# Revit family: Edge S - OX+
name_source: partatom
category: Doors
units: mm (PartAtom-declared; Revit-internal decimal feet)

## family parameters
Always vertical = Yes
Cut with Voids When Loaded = No
Host = Wall
OmniClass Number = 23.30.10.00
OmniClass Title = Doors
Room Calculation Point = No
Shared = No

## types (4) — shared parameters
Analytic Construction = <None>
Frame Projection Ext. = 1 "
Frame Projection Int. = 1 "
Frame Width = 3 "
Function = Interior
Height = 84 "
Interlocks and Single Blade = Yes
Keep and Fin Heights = 83.875 "
Panel Opening Height = 85 "
Rough Height = 89 "
Single Blade = Yes
Single Blade Height = 83 "
Single Blade Location = 1
Single Track Width = 2.5 "
Wall Closure = By host
Wall Setback = 2 "
zero-valued in all types: Thickness

## per-type parameters (varying)
| type | Center of Interlock Location | Interlocks and Fins | Net Panel Width | Number of Keeps | Number of Panels | Panel Opening Width | Panel Width | Recommended Wall Thickness | Rough Width | Single Blade Offset | Total Track Width | Width |
| OXX | 36.833 " | No | 112 " | 2 | 3 | 110 " | 37.333 " | 11.5 " | 111.375 " | 37.364 " | 7.5 " | 108 " |
| OXXX | 36.75 " | No | 149 " | 3 | 4 | 146 " | 37.25 " | 14 " | 147.375 " | 37.281 " | 10 " | 144 " |
| OXXXX | 36.7 " | No | 186 " | 4 | 5 | 182 " | 37.2 " | 16.5 " | 183.375 " | 37.231 " | 12.5 " | 180 " |
| OX | 37 " | Yes | 75 " | 1 | 2 | 74 " | 37.5 " | 9 " | 75.375 " | 37.531 " | 5 " | 72 " |

## geometry (parser evidence)
native form markers: Sweep x36
no freeform markers — native parametric forms only
